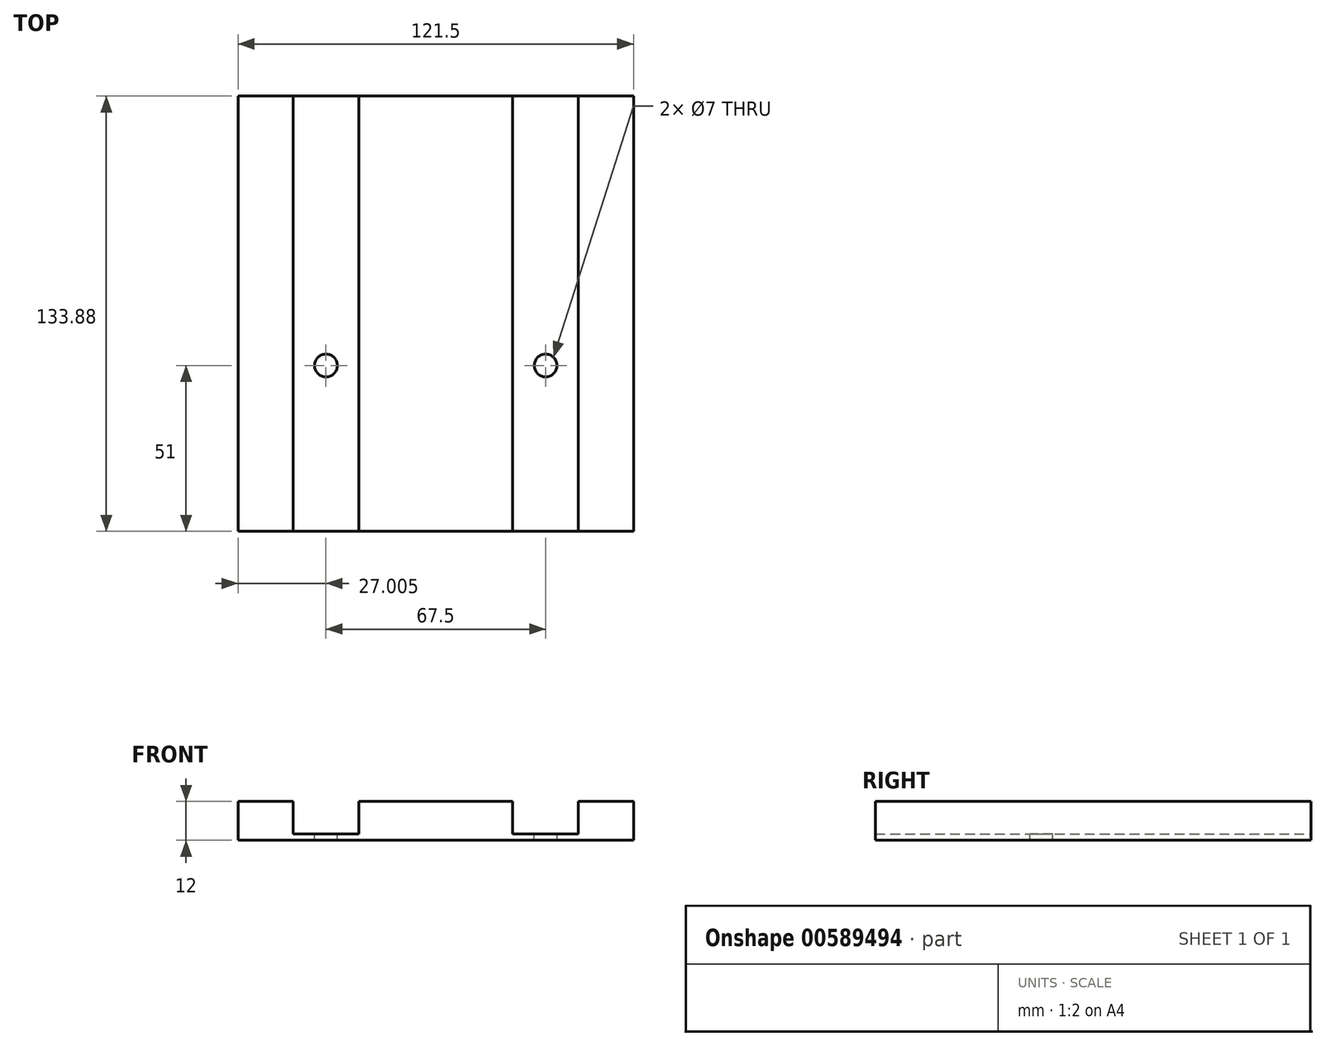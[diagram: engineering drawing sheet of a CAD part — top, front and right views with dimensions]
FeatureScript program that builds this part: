
annotation { "Feature Type Name" : "Feature", "Feature Type Description" : "" }
export const myFeature = defineFeature(function(context is Context, id is Id, definition is map)
    precondition{}
    {
        {
            var Q0;
            Q0=qCreatedBy(makeId("Front.planeOp"),FACE);
            var sketch = newSketch(context, id + "F0", { "sketchPlane" : qUnion([Q0])});
            skLineSegment(sketch, "E0", {"start": v(-45.83, 0) * mm, "end": v(41.67, 0) * mm});
            skLineSegment(sketch, "E1", {"start": v(-45.83, 0) * mm, "end": v(-45.83, 2) * mm});
            skLineSegment(sketch, "E2", {"start": v(41.67, 0) * mm, "end": v(41.67, 2) * mm});
            skLineSegment(sketch, "E3", {"start": v(-45.83, 2) * mm, "end": v(-25.83, 2) * mm});
            skLineSegment(sketch, "E4", {"start": v(41.67, 2) * mm, "end": v(21.67, 2) * mm});
            skLineSegment(sketch, "E5", {"start": v(-25.83, 2) * mm, "end": v(-25.83, 12) * mm});
            skLineSegment(sketch, "E6", {"start": v(21.67, 2) * mm, "end": v(21.67, 12) * mm});
            skLineSegment(sketch, "E7", {"start": v(-25.83, 12) * mm, "end": v(21.67, 12) * mm});
            skSolve(sketch);
        }
        {
            var Q0;
            Q0=makeQuery(id+"F0.imprint","IMPRINT",FACE,{"disambiguationData":[TD([[makeQuery(id+"F0.imprint","IMPRINT",EDGE,{"derivedFrom":sQuery(id+"F0.wireOp",EDGE,"E0")}),1.0]])]});
            extrude(context, id + "F1", {"entities" : qUnion([Q0]), "depth" : 250 * mm, "offsetDistance" : 25 * mm});
        }
        {
            var Q0;
            Q0=makeQuery(id+"F1.opExtrude","CAP_FACE",FACE,{"disambiguationData":[OSD([sQuery(id+"F0.wireOp",EDGE,"E0"),sQuery(id+"F0.wireOp",EDGE,"E1"),sQuery(id+"F0.wireOp",EDGE,"E2"),sQuery(id+"F0.wireOp",EDGE,"E3"),sQuery(id+"F0.wireOp",EDGE,"E4"),sQuery(id+"F0.wireOp",EDGE,"E5"),sQuery(id+"F0.wireOp",EDGE,"E6"),sQuery(id+"F0.wireOp",EDGE,"E7")])],"isStart":true});
            var sketch = newSketch(context, id + "F2", { "sketchPlane" : qUnion([Q0])});
            skLineSegment(sketch, "E8", {"start": v(-41.67, 0) * mm, "end": v(45.83, 0) * mm});
            skLineSegment(sketch, "E9", {"start": v(-41.67, 0) * mm, "end": v(-41.67, 12) * mm});
            skLineSegment(sketch, "E10", {"start": v(-41.67, 12) * mm, "end": v(45.83, 12) * mm});
            skLineSegment(sketch, "E11", {"start": v(45.83, 12) * mm, "end": v(45.83, 0) * mm});
            skSolve(sketch);
        }
        {
            var Q0;
            Q0 = qSketchRegion(id + "F2", true);
            extrude(context, id + "F3", {"entities" : qUnion([Q0]), "operationType" : NewBodyOperationType.ADD, "depth" : 20 * mm, "offsetDistance" : 25 * mm});
        }
        {
            var Q0;
            Q0=makeQuery(id+"F1.opExtrude","SWEPT_FACE",FACE,{"disambiguationData":[OSD([sQuery(id+"F0.wireOp",EDGE,"E4")])]});
            var sketch = newSketch(context, id + "F4", { "sketchPlane" : qUnion([Q0])});
            skPoint(sketch, "E12", {"position": v(31.67, -51) * mm});
            skPoint(sketch, "E12.positionSnap0", {"position": v(31.67, 0) * mm});
            skPoint(sketch, "E13", {"position": v(31.67, -199) * mm});
            skPoint(sketch, "E14", {"position": v(-35.83, -199) * mm});
            skPoint(sketch, "E15", {"position": v(-35.83, -51) * mm});
            skSolve(sketch);
        }
        {
            var Q0;
            Q0=sQuery(id+"F4.wireOp",VERTEX,"E15");
            var Q1;
            Q1=sQuery(id+"F4.wireOp",VERTEX,"E13");
            var Q2;
            Q2=sQuery(id+"F4.wireOp",VERTEX,"E12");
            var Q3;
            Q3=sQuery(id+"F4.wireOp",VERTEX,"E14");
            var Q4;
            Q4=makeQuery(id+"F1.opExtrude","SWEPT_BODY",BODY,{"disambiguationData":[OSD([sQuery(id+"F0.wireOp",EDGE,"E0"),sQuery(id+"F0.wireOp",EDGE,"E1"),sQuery(id+"F0.wireOp",EDGE,"E2"),sQuery(id+"F0.wireOp",EDGE,"E3"),sQuery(id+"F0.wireOp",EDGE,"E4"),sQuery(id+"F0.wireOp",EDGE,"E5"),sQuery(id+"F0.wireOp",EDGE,"E6"),sQuery(id+"F0.wireOp",EDGE,"E7")])]});
            hole(context, id + "F5", {"style" : HoleStyle.SIMPLE, "endStyle" : HoleEndStyle.BLIND, "holeDiameter" : 7 * mm, "majorDiameter" : 5 * mm, "holeDepth" : 40 * mm, "isTappedThrough" : true, "tappedDepth" : 12 * mm, "tapClearance" : 3, "locations" : qUnion([Q0, Q1, Q2, Q3]), "scope" : qUnion([Q4])});
        }
        {
            var Q0;
            Q0=makeQuery(id+"F3.boolean.opBoolean","MERGE",FACE,{"derivedFrom":[makeQuery(id+"F1.opExtrude","SWEPT_FACE",FACE,{"disambiguationData":[OSD([sQuery(id+"F0.wireOp",EDGE,"E2")])]}),makeQuery(id+"F3.opExtrude","SWEPT_FACE",FACE,{"disambiguationData":[OSD([sQuery(id+"F2.wireOp",EDGE,"E9")])]})]});
            var sketch = newSketch(context, id + "F6", { "sketchPlane" : qUnion([Q0])});
            skSolve(sketch);
        }
        {
            var Q0;
            Q0=makeQuery(id+"F3.boolean.opBoolean","MERGE",FACE,{"derivedFrom":[makeQuery(id+"F1.opExtrude","SWEPT_FACE",FACE,{"disambiguationData":[OSD([sQuery(id+"F0.wireOp",EDGE,"E1")])]}),makeQuery(id+"F3.opExtrude","SWEPT_FACE",FACE,{"disambiguationData":[OSD([sQuery(id+"F2.wireOp",EDGE,"E11")])]})]});
            extrude(context, id + "F7", {"entities" : qUnion([Q0]), "operationType" : NewBodyOperationType.ADD, "depth" : 17 * mm, "offsetDistance" : 25 * mm});
        }
        {
            var Q0;
            {var subQ1=sQuery(id+"F0.wireOp",EDGE,"E2");Q0=makeQuery(id+"F6.imprint","IMPRINT",FACE,{"disambiguationData":[TD([[makeQuery(id+"F6.imprint","IMPRINT",EDGE,{"derivedFrom":makeQuery(id+"F1.opExtrude","CAP_EDGE",EDGE,{"disambiguationData":[OSD([subQ1])],"isStart":false})}),-1.0]])]});}
            extrude(context, id + "F8", {"entities" : qUnion([Q0]), "operationType" : NewBodyOperationType.ADD, "depth" : 17 * mm, "offsetDistance" : 25 * mm});
        }
        {
            var Q0;
            {var subQ0=sQuery(id+"F0.wireOp",EDGE,"E4");Q0=makeQuery(id+"F8.boolean.opBoolean","MERGE",FACE,{"derivedFrom":[makeQuery(id+"F1.opExtrude","SWEPT_FACE",FACE,{"disambiguationData":[OSD([subQ0])]}),makeQuery(id+"F8.opExtrude","SWEPT_FACE",FACE,{"disambiguationData":[OSD([sQuery(id+"F0.wireOp",EDGE,"E2"),subQ0])]})]});}
            var sketch = newSketch(context, id + "F9", { "sketchPlane" : qUnion([Q0])});
            skLineSegment(sketch, "E16.bottom", {"start": v(58.67, 0) * mm, "end": v(41.77, 0) * mm});
            skLineSegment(sketch, "E16.top", {"start": v(58.67, -250) * mm, "end": v(41.77, -250) * mm});
            skLineSegment(sketch, "E16.left", {"start": v(58.67, 0) * mm, "end": v(58.67, -250) * mm});
            skLineSegment(sketch, "E16.right", {"start": v(41.77, 0) * mm, "end": v(41.77, -250) * mm});
            skSolve(sketch);
        }
        {
            var Q0;
            Q0=makeQuery(id+"F9.imprint","IMPRINT",FACE,{"disambiguationData":[TD([[makeQuery(id+"F9.imprint","IMPRINT",EDGE,{"derivedFrom":sQuery(id+"F9.wireOp",EDGE,"E16.bottom")}),1.0]])]});
            extrude(context, id + "F10", {"entities" : qUnion([Q0]), "operationType" : NewBodyOperationType.ADD, "depth" : 10 * mm, "offsetDistance" : 25 * mm});
        }
        {
            var Q0;
            {var subQ0=sQuery(id+"F0.wireOp",EDGE,"E3");Q0=makeQuery(id+"F7.boolean.opBoolean","MERGE",FACE,{"derivedFrom":[makeQuery(id+"F1.opExtrude","SWEPT_FACE",FACE,{"disambiguationData":[OSD([subQ0])]}),makeQuery(id+"F7.opExtrude","SWEPT_FACE",FACE,{"disambiguationData":[OSD([sQuery(id+"F0.wireOp",EDGE,"E1"),subQ0])]})]});}
            var sketch = newSketch(context, id + "F11", { "sketchPlane" : qUnion([Q0])});
            skLineSegment(sketch, "E17.bottom", {"start": v(-62.83, 0) * mm, "end": v(-45.93, 0) * mm});
            skLineSegment(sketch, "E17.top", {"start": v(-62.83, -250) * mm, "end": v(-45.93, -250) * mm});
            skLineSegment(sketch, "E17.left", {"start": v(-62.83, 0) * mm, "end": v(-62.83, -250) * mm});
            skLineSegment(sketch, "E17.right", {"start": v(-45.93, 0) * mm, "end": v(-45.93, -250) * mm});
            skSolve(sketch);
        }
        {
            var Q0;
            Q0=makeQuery(id+"F11.imprint","IMPRINT",FACE,{"disambiguationData":[TD([[makeQuery(id+"F11.imprint","IMPRINT",EDGE,{"derivedFrom":sQuery(id+"F11.wireOp",EDGE,"E17.bottom")}),-1.0]])]});
            extrude(context, id + "F12", {"entities" : qUnion([Q0]), "operationType" : NewBodyOperationType.ADD, "depth" : 10 * mm, "offsetDistance" : 25 * mm});
        }
        {
            var Q0;
            {var subQ0=sQuery(id+"F2.wireOp",EDGE,"E10");Q0=makeQuery(id+"F12.boolean.opBoolean","MERGE",FACE,{"derivedFrom":[makeQuery(id+"F10.boolean.opBoolean","MERGE",FACE,{"derivedFrom":[makeQuery(id+"F8.boolean.opBoolean","MERGE",FACE,{"derivedFrom":[makeQuery(id+"F7.boolean.opBoolean","MERGE",FACE,{"derivedFrom":[makeQuery(id+"F3.boolean.opBoolean","MERGE",FACE,{"derivedFrom":[makeQuery(id+"F1.opExtrude","SWEPT_FACE",FACE,{"disambiguationData":[OSD([sQuery(id+"F0.wireOp",EDGE,"E7")])]}),makeQuery(id+"F3.opExtrude","SWEPT_FACE",FACE,{"disambiguationData":[OSD([subQ0])]})]}),makeQuery(id+"F7.opExtrude","SWEPT_FACE",FACE,{"disambiguationData":[OSD([subQ0,sQuery(id+"F2.wireOp",EDGE,"E11")])]})]}),makeQuery(id+"F8.opExtrude","SWEPT_FACE",FACE,{"disambiguationData":[OSD([sQuery(id+"F2.wireOp",EDGE,"E9"),subQ0])]})]}),makeQuery(id+"F10.opExtrude","CAP_FACE",FACE,{"disambiguationData":[OSD([sQuery(id+"F9.wireOp",EDGE,"E16.bottom"),sQuery(id+"F9.wireOp",EDGE,"E16.top"),sQuery(id+"F9.wireOp",EDGE,"E16.left"),sQuery(id+"F9.wireOp",EDGE,"E16.right")])],"isStart":false})]}),makeQuery(id+"F12.opExtrude","CAP_FACE",FACE,{"disambiguationData":[OSD([sQuery(id+"F11.wireOp",EDGE,"E17.bottom"),sQuery(id+"F11.wireOp",EDGE,"E17.top"),sQuery(id+"F11.wireOp",EDGE,"E17.left"),sQuery(id+"F11.wireOp",EDGE,"E17.right")])],"isStart":false})]});}
            var sketch = newSketch(context, id + "F13", { "sketchPlane" : qUnion([Q0])});
            skArc(sketch, "E18", {"start": v(58.67, 0) * mm, "mid": v(-2.08, 20.2) * mm, "end": v(-62.83, 0) * mm});
            skSolve(sketch);
        }
        {
            var Q0;
            {var subQ0=sQuery(id+"F13.wireOp",EDGE,"E18");var subQ1=sQuery(id+"F2.wireOp",EDGE,"E11");var subQ2=sQuery(id+"F2.wireOp",EDGE,"E10");var subQ3=makeQuery(id+"F12.boolean.opBoolean","MERGE",EDGE,{"derivedFrom":[makeQuery(id+"F7.opExtrude","CAP_EDGE",EDGE,{"disambiguationData":[OSD([subQ2,subQ1])],"isStart":false}),makeQuery(id+"F12.opExtrude","CAP_EDGE",EDGE,{"disambiguationData":[OSD([sQuery(id+"F11.wireOp",EDGE,"E17.left")])],"isStart":false})]});var subQ4=makeQuery(id+"F13.imprint","INTERSECT",VERTEX,{"derivedFrom":[subQ3,subQ0]});Q0=makeQuery(id+"F13.imprint","IMPRINT",FACE,{"disambiguationData":[TD([[makeQuery(id+"F13.imprint","IMPRINT",EDGE,{"disambiguationData":[TD([[subQ4,1.0]])],"derivedFrom":subQ0}),-1.0]])]});}
            var Q1;
            {var subQ0=sQuery(id+"F13.wireOp",EDGE,"E18");var subQ1=sQuery(id+"F2.wireOp",EDGE,"E10");var subQ2=sQuery(id+"F2.wireOp",EDGE,"E9");var subQ3=makeQuery(id+"F10.boolean.opBoolean","MERGE",EDGE,{"derivedFrom":[makeQuery(id+"F8.opExtrude","CAP_EDGE",EDGE,{"disambiguationData":[OSD([subQ2,subQ1])],"isStart":false}),makeQuery(id+"F10.opExtrude","CAP_EDGE",EDGE,{"disambiguationData":[OSD([sQuery(id+"F9.wireOp",EDGE,"E16.left")])],"isStart":false})]});var subQ4=makeQuery(id+"F13.imprint","INTERSECT",VERTEX,{"derivedFrom":[subQ3,subQ0]});Q1=makeQuery(id+"F13.imprint","IMPRINT",FACE,{"disambiguationData":[TD([[makeQuery(id+"F13.imprint","IMPRINT",EDGE,{"disambiguationData":[TD([[subQ4,-1.0]])],"derivedFrom":subQ0}),-1.0]])]});}
            extrude(context, id + "F14", {"entities" : qUnion([Q0, Q1]), "operationType" : NewBodyOperationType.REMOVE, "oppositeDirection" : true, "depth" : 25 * mm, "offsetDistance" : 25 * mm});
        }
        {
            var Q0;
            {var subQ0=sQuery(id+"F13.wireOp",EDGE,"E18");var subQ1=sQuery(id+"F2.wireOp",EDGE,"E11");var subQ2=sQuery(id+"F2.wireOp",EDGE,"E10");Q0=makeQuery(id+"F14.boolean.opBoolean","COPY",EDGE,{"derivedFrom":makeQuery(id+"F14.opExtrude","CAP_EDGE",EDGE,{"disambiguationData":[OSD([subQ0]),TDD([makeQuery(id+"F13.imprint","IMPRINT",EDGE,{"disambiguationData":[TD([[makeQuery(id+"F13.imprint","INTERSECT",VERTEX,{"derivedFrom":[makeQuery(id+"F12.boolean.opBoolean","MERGE",EDGE,{"derivedFrom":[makeQuery(id+"F7.opExtrude","CAP_EDGE",EDGE,{"disambiguationData":[OSD([subQ2,subQ1])],"isStart":false}),makeQuery(id+"F12.opExtrude","CAP_EDGE",EDGE,{"disambiguationData":[OSD([sQuery(id+"F11.wireOp",EDGE,"E17.left")])],"isStart":false})]}),subQ0]}),1.0]])],"derivedFrom":subQ0})])],"isStart":true})});}
            var Q1;
            {var subQ0=sQuery(id+"F2.wireOp",EDGE,"E9");var subQ1=sQuery(id+"F2.wireOp",EDGE,"E10");var subQ2=sQuery(id+"F2.wireOp",EDGE,"E11");Q1=makeQuery(id+"F8.boolean.opBoolean","MERGE",EDGE,{"derivedFrom":[makeQuery(id+"F7.boolean.opBoolean","MERGE",EDGE,{"derivedFrom":[makeQuery(id+"F3.opExtrude","CAP_EDGE",EDGE,{"disambiguationData":[OSD([subQ1])],"isStart":false}),makeQuery(id+"F7.opExtrude","SWEPT_EDGE",EDGE,{"disambiguationData":[OSD([subQ1,subQ2]),TDD([makeQuery(id+"F3.opExtrude","CAP_VERTEX",VERTEX,{"disambiguationData":[OSD([subQ1,subQ2])],"isStart":false})])]})]}),makeQuery(id+"F8.opExtrude","SWEPT_EDGE",EDGE,{"disambiguationData":[OSD([subQ0,subQ1]),TDD([makeQuery(id+"F6.imprint","INTERSECT",VERTEX,{"derivedFrom":[makeQuery(id+"F3.opExtrude","SWEPT_EDGE",EDGE,{"disambiguationData":[OSD([subQ0,subQ1])]}),makeQuery(id+"F3.opExtrude","CAP_EDGE",EDGE,{"disambiguationData":[OSD([subQ0])],"isStart":false})]})])]})]});}
            var Q2;
            {var subQ0=sQuery(id+"F13.wireOp",EDGE,"E18");var subQ1=sQuery(id+"F2.wireOp",EDGE,"E10");var subQ2=sQuery(id+"F2.wireOp",EDGE,"E9");Q2=makeQuery(id+"F14.boolean.opBoolean","COPY",EDGE,{"derivedFrom":makeQuery(id+"F14.opExtrude","CAP_EDGE",EDGE,{"disambiguationData":[OSD([subQ0]),TDD([makeQuery(id+"F13.imprint","IMPRINT",EDGE,{"disambiguationData":[TD([[makeQuery(id+"F13.imprint","INTERSECT",VERTEX,{"derivedFrom":[makeQuery(id+"F10.boolean.opBoolean","MERGE",EDGE,{"derivedFrom":[makeQuery(id+"F8.opExtrude","CAP_EDGE",EDGE,{"disambiguationData":[OSD([subQ2,subQ1])],"isStart":false}),makeQuery(id+"F10.opExtrude","CAP_EDGE",EDGE,{"disambiguationData":[OSD([sQuery(id+"F9.wireOp",EDGE,"E16.left")])],"isStart":false})]}),subQ0]}),-1.0]])],"derivedFrom":subQ0})])],"isStart":true})});}
            fillet(context, id + "F15", {"entities" : qUnion([Q0, Q1, Q2]), "radius" : 5 * mm, "tangentPropagation" : true, "allowEdgeOverflow" : false});
        }
        {
            var Q0;
            Q0=makeQuery(id+"F12.boolean.opBoolean","MERGE",FACE,{"derivedFrom":[makeQuery(id+"F7.opExtrude","CAP_FACE",FACE,{"disambiguationData":[OSD([sQuery(id+"F0.wireOp",EDGE,"E1"),sQuery(id+"F2.wireOp",EDGE,"E11")])],"isStart":false}),makeQuery(id+"F12.opExtrude","SWEPT_FACE",FACE,{"disambiguationData":[OSD([sQuery(id+"F11.wireOp",EDGE,"E17.left")])]})]});
            cPlane(context, id + "F16", {"entities" : qUnion([Q0]), "cplaneType" : CPlaneType.OFFSET, "offset" : 25 * mm, "width" : 150 * mm, "height" : 150 * mm});
        }
        {
            var Q0;
            Q0=qCreatedBy(id+"F16.planeOp",FACE);
            cPlane(context, id + "F17", {"entities" : qUnion([Q0]), "cplaneType" : CPlaneType.OFFSET, "offset" : 25 * mm, "width" : 150 * mm, "height" : 150 * mm});
        }
        {
            var Q0;
            Q0=makeQuery(id+"F1.opExtrude","SWEPT_FACE",FACE,{"disambiguationData":[OSD([sQuery(id+"F0.wireOp",EDGE,"E6")])]});
            var sketch = newSketch(context, id + "F18", { "sketchPlane" : qUnion([Q0])});
            skSolve(sketch);
        }
        {
            var Q0;
            Q0 = qSketchRegion(id + "F18", true);
            var Q1;
            {var subQ0=sQuery(id+"F0.wireOp",EDGE,"E6");Q1=makeQuery(id+"F18.imprint","IMPRINT",FACE,{"disambiguationData":[TD([[makeQuery(id+"F18.imprint","IMPRINT",EDGE,{"derivedFrom":makeQuery(id+"F1.opExtrude","CAP_EDGE",EDGE,{"disambiguationData":[OSD([subQ0])],"isStart":false})}),-1.0]])]});}
            extrude(context, id + "F19", {"entities" : qUnion([Q0, Q1]), "operationType" : NewBodyOperationType.REMOVE, "oppositeDirection" : true, "depth" : 0.1 * mm, "offsetDistance" : 25 * mm});
        }
        {
            var Q0;
            Q0=makeQuery(id+"F1.opExtrude","SWEPT_FACE",FACE,{"disambiguationData":[OSD([sQuery(id+"F0.wireOp",EDGE,"E5")])]});
            var sketch = newSketch(context, id + "F20", { "sketchPlane" : qUnion([Q0])});
            skSolve(sketch);
        }
        {
            var Q0;
            Q0 = qSketchRegion(id + "F20", true);
            var Q1;
            {var subQ0=sQuery(id+"F0.wireOp",EDGE,"E5");Q1=makeQuery(id+"F20.imprint","IMPRINT",FACE,{"disambiguationData":[TD([[makeQuery(id+"F20.imprint","IMPRINT",EDGE,{"derivedFrom":makeQuery(id+"F1.opExtrude","CAP_EDGE",EDGE,{"disambiguationData":[OSD([subQ0])],"isStart":false})}),1.0]])]});}
            extrude(context, id + "F21", {"entities" : qUnion([Q0, Q1]), "operationType" : NewBodyOperationType.REMOVE, "oppositeDirection" : true, "depth" : 0.1 * mm, "offsetDistance" : 25 * mm});
        }
        {
            var Q0;
            Q0=qCreatedBy(id+"F17.planeOp",FACE);
            var sketch = newSketch(context, id + "F22", { "sketchPlane" : qUnion([Q0])});
            skLineSegment(sketch, "E19.bottom", {"start": v(116.12, 37) * mm, "end": v(-27.46, 37) * mm});
            skLineSegment(sketch, "E19.top", {"start": v(116.12, -26.7) * mm, "end": v(-27.46, -26.7) * mm});
            skLineSegment(sketch, "E19.left", {"start": v(116.12, 37) * mm, "end": v(116.12, -26.7) * mm});
            skLineSegment(sketch, "E19.right", {"start": v(-27.46, 37) * mm, "end": v(-27.46, -26.7) * mm});
            skSolve(sketch);
        }
        {
            var Q0;
            Q0=makeQuery(id+"F22.imprint","IMPRINT",FACE,{"disambiguationData":[TD([[makeQuery(id+"F22.imprint","IMPRINT",EDGE,{"derivedFrom":sQuery(id+"F22.wireOp",EDGE,"E19.bottom")}),1.0]])]});
            extrude(context, id + "F23", {"entities" : qUnion([Q0]), "operationType" : NewBodyOperationType.REMOVE, "oppositeDirection" : true, "depth" : 259 * mm, "offsetDistance" : 25 * mm});
        }
    });
